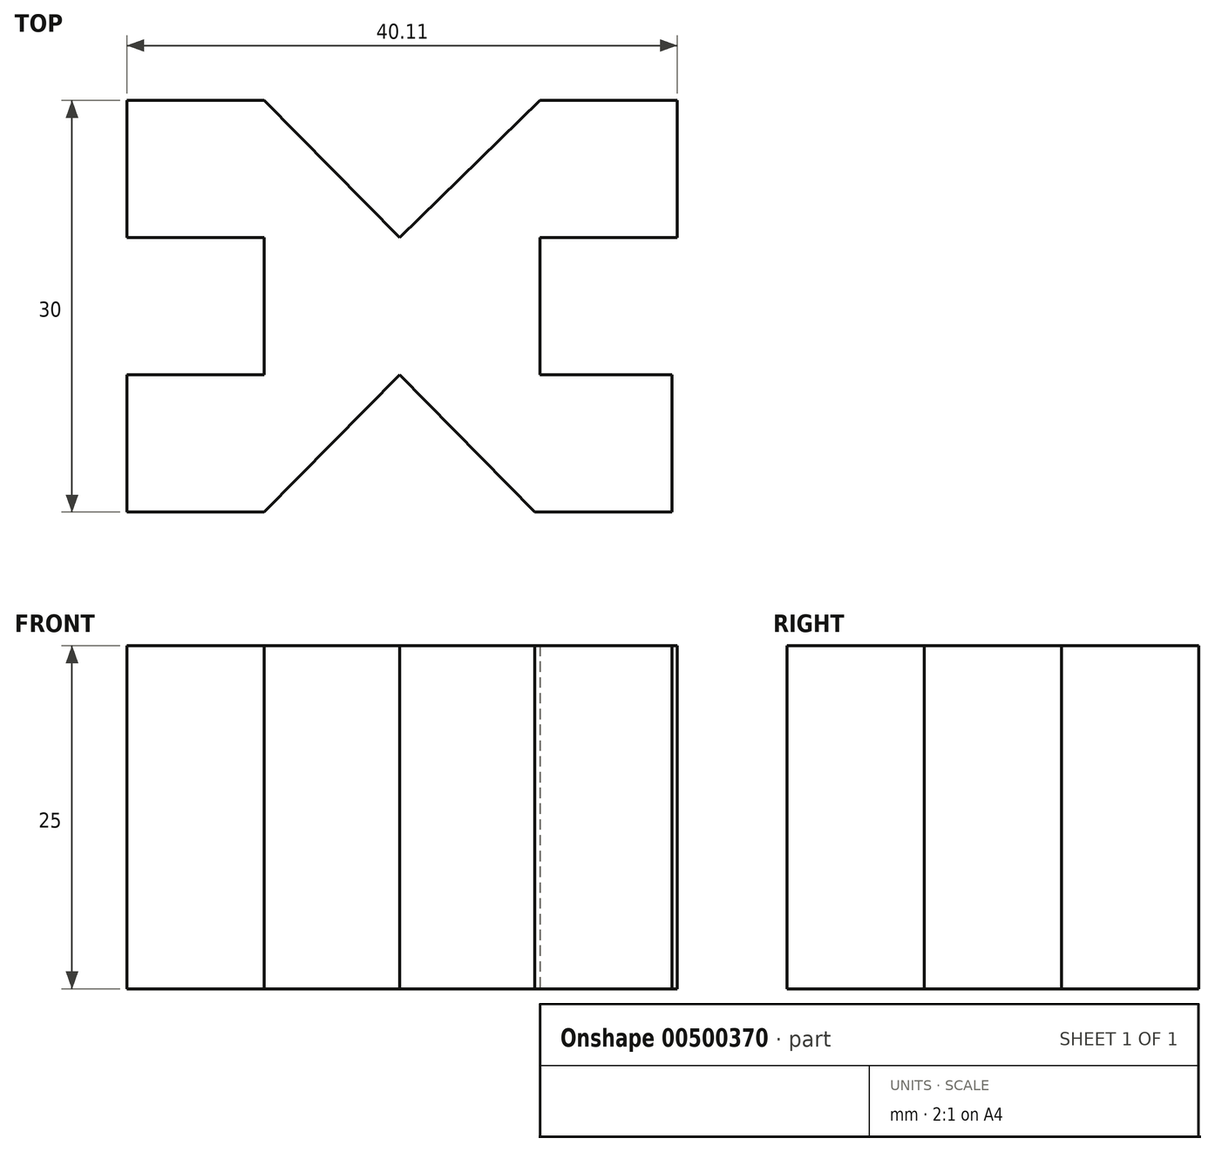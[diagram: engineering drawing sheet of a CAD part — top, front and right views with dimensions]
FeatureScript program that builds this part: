
annotation { "Feature Type Name" : "Feature", "Feature Type Description" : "" }
export const myFeature = defineFeature(function(context is Context, id is Id, definition is map)
    precondition{}
    {
        {
            var Q0;
            Q0=qCreatedBy(makeId("Top.planeOp"),FACE);
            var sketch = newSketch(context, id + "F0", { "sketchPlane" : qUnion([Q0])});
            skLineSegment(sketch, "E0", {"start": v(0, 0) * mm, "end": v(-9.86, 10) * mm});
            skLineSegment(sketch, "E1", {"start": v(-9.86, 10) * mm, "end": v(-19.86, 10) * mm});
            skLineSegment(sketch, "E2", {"start": v(-19.86, 10) * mm, "end": v(-19.86, 0) * mm});
            skLineSegment(sketch, "E3", {"start": v(-19.86, 0) * mm, "end": v(-9.86, 0) * mm});
            skLineSegment(sketch, "E4", {"start": v(-9.86, 0) * mm, "end": v(-9.86, -10) * mm});
            skLineSegment(sketch, "E5", {"start": v(-9.86, -10) * mm, "end": v(-19.86, -10) * mm});
            skLineSegment(sketch, "E6", {"start": v(-19.86, -10) * mm, "end": v(-19.86, -20) * mm});
            skLineSegment(sketch, "E7", {"start": v(-19.86, -20) * mm, "end": v(-9.86, -20) * mm});
            skLineSegment(sketch, "E8", {"start": v(-9.86, -20) * mm, "end": v(0, -10) * mm});
            skLineSegment(sketch, "E9", {"start": v(0, -10) * mm, "end": v(9.85, -20) * mm});
            skLineSegment(sketch, "E10", {"start": v(9.85, -20) * mm, "end": v(19.85, -20) * mm});
            skLineSegment(sketch, "E11", {"start": v(19.85, -20) * mm, "end": v(19.85, -10) * mm});
            skLineSegment(sketch, "E12", {"start": v(19.85, -10) * mm, "end": v(10.25, -10) * mm});
            skLineSegment(sketch, "E13", {"start": v(10.25, -10) * mm, "end": v(10.25, 0) * mm});
            skLineSegment(sketch, "E14", {"start": v(10.25, 0) * mm, "end": v(20.25, 0) * mm});
            skLineSegment(sketch, "E15", {"start": v(20.25, 0) * mm, "end": v(20.25, 10) * mm});
            skLineSegment(sketch, "E16", {"start": v(20.25, 10) * mm, "end": v(10.25, 10) * mm});
            skLineSegment(sketch, "E17", {"start": v(10.25, 10) * mm, "end": v(0, 0) * mm});
            skSolve(sketch);
        }
        {
            var Q0;
            Q0=makeQuery(id+"F0.imprint","IMPRINT",FACE,{"disambiguationData":[TD([[makeQuery(id+"F0.imprint","IMPRINT",EDGE,{"derivedFrom":sQuery(id+"F0.wireOp",EDGE,"E0")}),1.0]])]});
            extrude(context, id + "F1", {"entities" : qUnion([Q0]), "depth" : 25 * mm});
        }
    });
